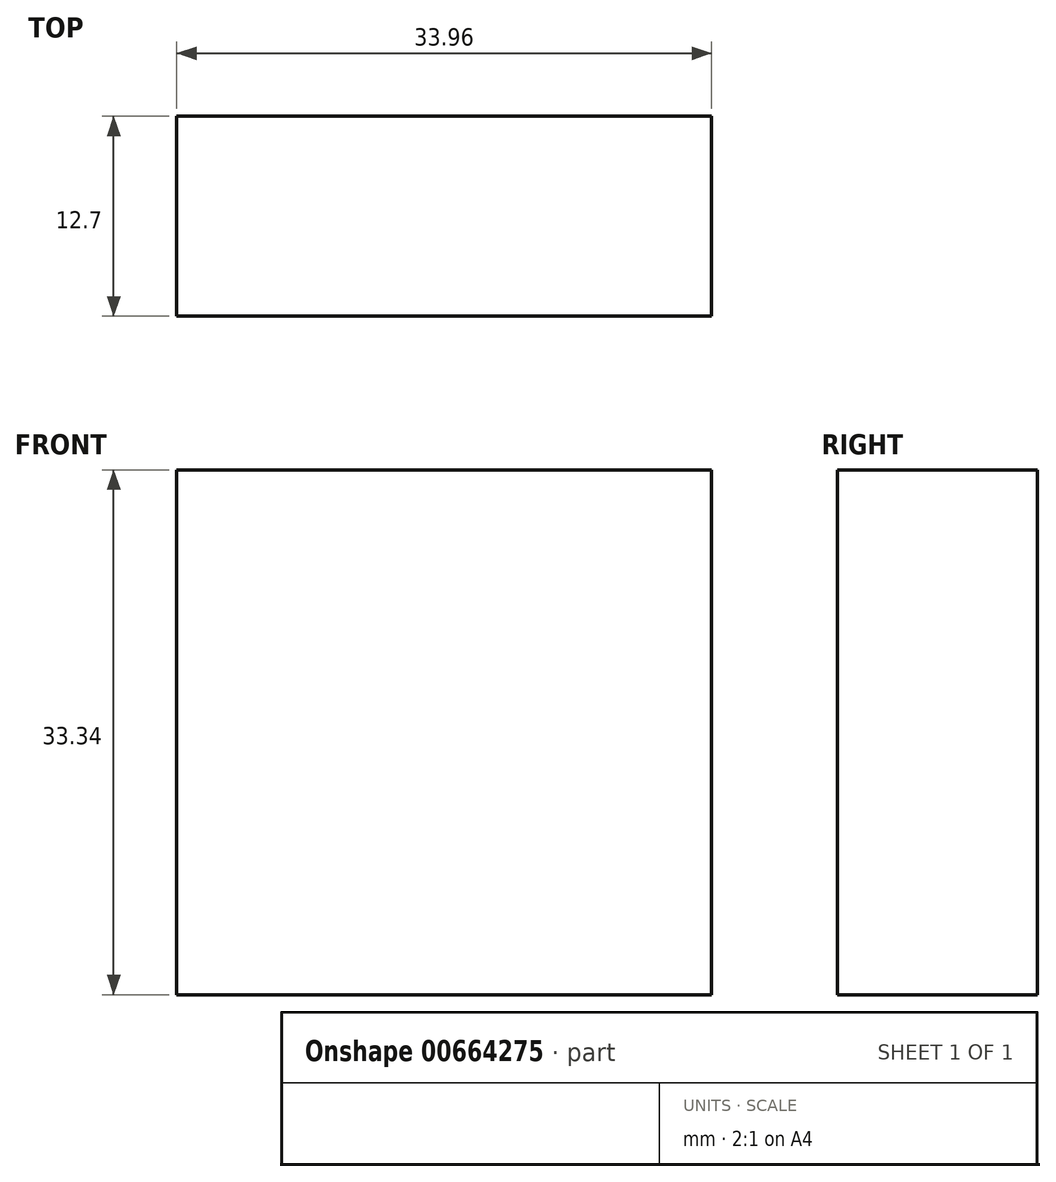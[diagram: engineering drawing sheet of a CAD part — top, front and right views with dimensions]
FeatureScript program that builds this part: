
annotation { "Feature Type Name" : "Feature", "Feature Type Description" : "" }
export const myFeature = defineFeature(function(context is Context, id is Id, definition is map)
    precondition{}
    {
        {
            var Q0;
            Q0=qCreatedBy(makeId("Front.planeOp"),FACE);
            var sketch = newSketch(context, id + "F0", { "sketchPlane" : qUnion([Q0])});
            skLineSegment(sketch, "E0.bottom", {"start": v(0, 0) * mm, "end": v(33.96, 0) * mm});
            skLineSegment(sketch, "E0.top", {"start": v(0, 33.34) * mm, "end": v(33.96, 33.34) * mm});
            skLineSegment(sketch, "E0.left", {"start": v(0, 0) * mm, "end": v(0, 33.34) * mm});
            skLineSegment(sketch, "E0.right", {"start": v(33.96, 0) * mm, "end": v(33.96, 33.34) * mm});
            skSolve(sketch);
        }
        {
            var Q0;
            Q0=makeQuery(id+"F0.imprint","IMPRINT",FACE,{"disambiguationData":[TD([[makeQuery(id+"F0.imprint","IMPRINT",EDGE,{"derivedFrom":sQuery(id+"F0.wireOp",EDGE,"E0.bottom")}),1.0]])]});
            extrude(context, id + "F1", {"entities" : qUnion([Q0]), "depth" : 12.7 * mm, "offsetDistance" : 25.4 * mm});
        }
    });
